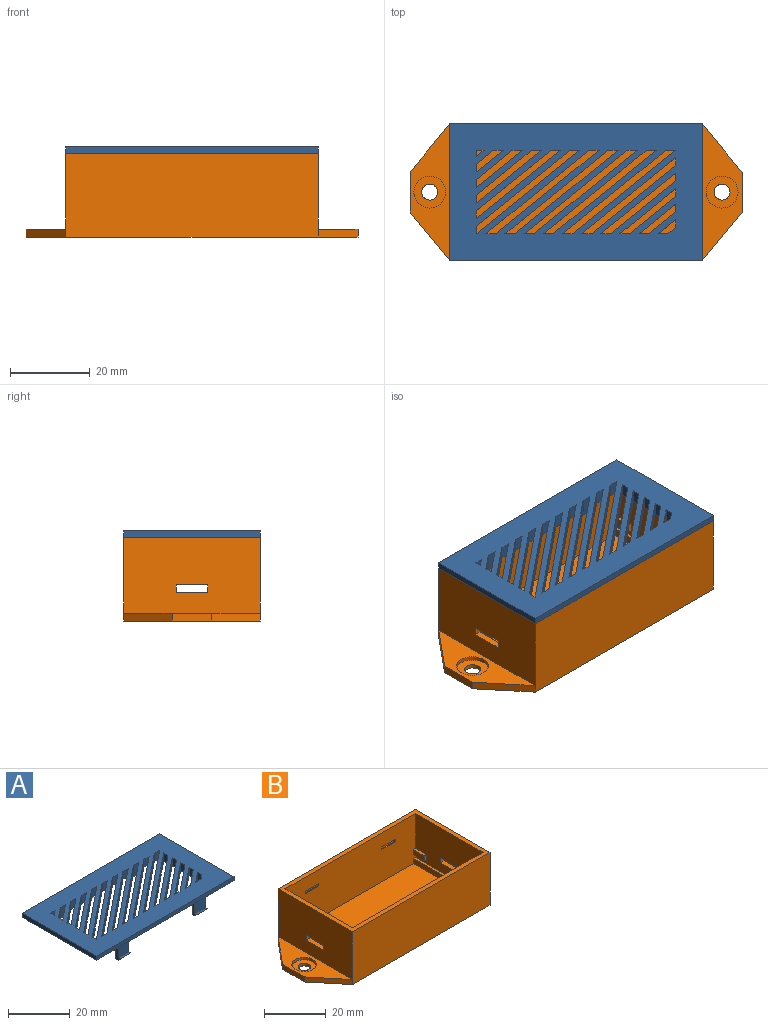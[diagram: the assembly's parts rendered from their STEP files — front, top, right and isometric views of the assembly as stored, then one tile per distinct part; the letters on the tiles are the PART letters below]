
ASSEMBLY  parts=2 mates=1
PART A: 98 faces, bbox 63.2x34.2x8.2 mm
  f0: plane 60x31mm, normal (0,0,-1), area 1312mm2, adj f2,f3,f9,f10,f11,f12,f13,f15
  f1: plane 63.2x34.2mm, normal (0,0,1), area 1636.4mm2, adj f5,f6,f7,f8,f35,f36,f37,f38
  f2: plane 60x5.6mm, normal (0,1,0), area 134.4mm2, adj f0,f4,f9,f10,f19,f21,f23,f24
  f3: plane 60x5.6mm, normal (0,-1,0), area 134.4mm2, adj f0,f4,f9,f10,f11,f13,f15,f16
  f4: plane 63.2x34.2mm, normal (0,0,-1), area 301.4mm2, adj f2,f3,f5,f6,f7,f8,f9,f10
  f5: plane 63.2x1.6mm, normal (0,-1,0), area 101.1mm2, adj f1,f4,f6,f8
  f6: plane 34.2x1.6mm, normal (1,0,0), area 54.7mm2, adj f1,f4,f5,f7
  f7: plane 63.2x1.6mm, normal (0,1,0), area 101.1mm2, adj f1,f4,f6,f8
  f8: plane 34.2x1.6mm, normal (-1,0,0), area 54.7mm2, adj f1,f4,f5,f7
  f9: plane 31x1.6mm, normal (1,0,0), area 49.6mm2, adj f0,f2,f3,f4
  f10: plane 31x1.6mm, normal (-1,0,0), area 49.6mm2, adj f0,f2,f3,f4
  f11: plane 5x2.2mm, normal (-1,0,0), area 6.5mm2, adj f0,f3,f12,f14,f33,f34
  f12: plane 5x4.8mm, normal (0,1,0), area 24mm2, adj f0,f11,f13,f14
  f13: plane 5x2.2mm, normal (1,0,0), area 6.5mm2, adj f0,f3,f12,f14,f33,f34
  f14: plane 4.8x1.2mm, normal (0,0,-1), area 5.8mm2, adj f11,f12,f13,f34
  f15: plane 5x2.2mm, normal (1,0,0), area 6.5mm2, adj f0,f3,f17,f18,f27,f28
  f16: plane 5x2.2mm, normal (-1,0,0), area 6.5mm2, adj f0,f3,f17,f18,f27,f28
  f17: plane 5x4.8mm, normal (0,1,0), area 24mm2, adj f0,f15,f16,f18
  f18: plane 4.8x1.2mm, normal (0,0,-1), area 5.8mm2, adj f15,f16,f17,f28
  f19: plane 5x2.2mm, normal (1,0,0), area 6.5mm2, adj f0,f2,f20,f22,f29,f30
  f20: plane 5x4.8mm, normal (0,-1,0), area 24mm2, adj f0,f19,f21,f22
  f21: plane 5x2.2mm, normal (-1,0,0), area 6.5mm2, adj f0,f2,f20,f22,f29,f30
  f22: plane 4.8x1.2mm, normal (0,0,-1), area 5.8mm2, adj f19,f20,f21,f30
  f23: plane 5x2.2mm, normal (-1,0,0), area 6.5mm2, adj f0,f2,f25,f26,f31,f32
  f24: plane 5x2.2mm, normal (1,0,0), area 6.5mm2, adj f0,f2,f25,f26,f31,f32
  f25: plane 5x4.8mm, normal (0,-1,0), area 24mm2, adj f0,f23,f24,f26
  f26: plane 4.8x1.2mm, normal (0,0,-1), area 5.8mm2, adj f23,f24,f25,f32
  f27: plane 4.8x1mm, normal (0,0,1), area 4.8mm2, adj f3,f15,f16,f28
  f28: plane 4.8x1mm, normal (0,-0.71,-0.71), area 6.8mm2, adj f15,f16,f18,f27
  f29: plane 4.8x1mm, normal (0,0,1), area 4.8mm2, adj f2,f19,f21,f30
  f30: plane 4.8x1mm, normal (0,0.71,-0.71), area 6.8mm2, adj f19,f21,f22,f29
  f31: plane 4.8x1mm, normal (0,0,1), area 4.8mm2, adj f2,f23,f24,f32
  f32: plane 4.8x1mm, normal (0,0.71,-0.71), area 6.8mm2, adj f23,f24,f26,f31
  f33: plane 4.8x1mm, normal (0,0,1), area 4.8mm2, adj f3,f11,f13,f34
  f34: plane 4.8x1mm, normal (0,-0.71,-0.71), area 6.8mm2, adj f11,f13,f14,f33
  f35: plane 3.2x2mm, normal (-0.63,0.78,0), area 8.2mm2, adj f0,f1,f36,f37
  f36: plane 3.2x1.62mm, normal (1,0,0), area 5.2mm2, adj f0,f1,f35,f37
  f37: plane 3.2x2mm, normal (0,-1,0), area 6.4mm2, adj f0,f1,f35,f36
  f38: plane 3.2x2.4mm, normal (0,1,0), area 7.7mm2, adj f0,f1,f39,f41
  f39: plane 23.6x19.06mm, normal (0.63,-0.78,0), area 97.1mm2, adj f0,f1,f38,f40
  f40: plane 3.2x1.94mm, normal (-1,0,0), area 6.2mm2, adj f0,f1,f39,f41
  f41: plane 21.2x17.12mm, normal (-0.63,0.78,0), area 87.2mm2, adj f0,f1,f38,f40
  f42: plane 3.2x2.4mm, normal (0,1,0), area 7.7mm2, adj f0,f1,f43,f45
  f43: plane 18.8x15.18mm, normal (0.63,-0.78,0), area 77.3mm2, adj f0,f1,f42,f44
  f44: plane 3.2x1.94mm, normal (-1,0,0), area 6.2mm2, adj f0,f1,f43,f45
  f45: plane 16.4x13.25mm, normal (-0.63,0.78,0), area 67.5mm2, adj f0,f1,f42,f44
  f46: plane 3.2x2.4mm, normal (0,1,0), area 7.7mm2, adj f0,f1,f47,f49
  f47: plane 26x21mm, normal (0.63,-0.78,0), area 106.9mm2, adj f0,f1,f46,f48
  f48: plane 3.2x2.4mm, normal (0,-1,0), area 7.7mm2, adj f0,f1,f47,f49
  f49: plane 26x21mm, normal (-0.63,0.78,0), area 106.9mm2, adj f0,f1,f46,f48
  f50: plane 26x21mm, normal (-0.63,0.78,0), area 106.9mm2, adj f0,f1,f51,f53
  f51: plane 3.2x2.4mm, normal (0,1,0), area 7.7mm2, adj f0,f1,f50,f52
  f52: plane 26x21mm, normal (0.63,-0.78,0), area 106.9mm2, adj f0,f1,f51,f53
  f53: plane 3.2x2.4mm, normal (0,-1,0), area 7.7mm2, adj f0,f1,f50,f52
  f54: plane 3.2x2.4mm, normal (0,1,0), area 7.7mm2, adj f0,f1,f55,f57
  f55: plane 4.4x3.55mm, normal (0.63,-0.78,0), area 18.1mm2, adj f0,f1,f54,f56
  f56: plane 3.2x1.94mm, normal (-1,0,0), area 6.2mm2, adj f0,f1,f55,f57
  f57: plane 3.2x2mm, normal (-0.63,0.78,0), area 8.2mm2, adj f0,f1,f54,f56
  f58: plane 3.2x2.4mm, normal (0,1,0), area 7.7mm2, adj f0,f1,f59,f61
  f59: plane 14x11.31mm, normal (0.63,-0.78,0), area 57.6mm2, adj f0,f1,f58,f60
  f60: plane 3.2x1.94mm, normal (-1,0,0), area 6.2mm2, adj f0,f1,f59,f61
  f61: plane 11.6x9.37mm, normal (-0.63,0.78,0), area 47.7mm2, adj f0,f1,f58,f60
  f62: plane 3.2x2.4mm, normal (0,1,0), area 7.7mm2, adj f0,f1,f63,f65
  f63: plane 9.2x7.43mm, normal (0.63,-0.78,0), area 37.8mm2, adj f0,f1,f62,f64
  f64: plane 3.2x1.94mm, normal (-1,0,0), area 6.2mm2, adj f0,f1,f63,f65
  f65: plane 6.8x5.49mm, normal (-0.63,0.78,0), area 28mm2, adj f0,f1,f62,f64
  f66: plane 14x11.31mm, normal (0.63,-0.78,0), area 57.6mm2, adj f0,f1,f67,f69
  f67: plane 3.2x2.4mm, normal (0,-1,0), area 7.7mm2, adj f0,f1,f66,f68
  f68: plane 16.4x13.25mm, normal (-0.63,0.78,0), area 67.5mm2, adj f0,f1,f67,f69
  f69: plane 3.2x1.94mm, normal (1,0,0), area 6.2mm2, adj f0,f1,f66,f68
  f70: plane 18.8x15.18mm, normal (0.63,-0.78,0), area 77.3mm2, adj f0,f1,f71,f73
  f71: plane 3.2x2.4mm, normal (0,-1,0), area 7.7mm2, adj f0,f1,f70,f72
  f72: plane 21.2x17.12mm, normal (-0.63,0.78,0), area 87.2mm2, adj f0,f1,f71,f73
  f73: plane 3.2x1.94mm, normal (1,0,0), area 6.2mm2, adj f0,f1,f70,f72
  f74: plane 4.4x3.55mm, normal (0.63,-0.78,0), area 18.1mm2, adj f0,f1,f75,f77
  f75: plane 3.2x2.4mm, normal (0,-1,0), area 7.7mm2, adj f0,f1,f74,f76
  f76: plane 6.8x5.49mm, normal (-0.63,0.78,0), area 28mm2, adj f0,f1,f75,f77
  f77: plane 3.2x1.94mm, normal (1,0,0), area 6.2mm2, adj f0,f1,f74,f76
  f78: plane 9.2x7.43mm, normal (0.63,-0.78,0), area 37.8mm2, adj f0,f1,f79,f81
  f79: plane 3.2x2.4mm, normal (0,-1,0), area 7.7mm2, adj f0,f1,f78,f80
  f80: plane 11.6x9.37mm, normal (-0.63,0.78,0), area 47.7mm2, adj f0,f1,f79,f81
  f81: plane 3.2x1.94mm, normal (1,0,0), area 6.2mm2, adj f0,f1,f78,f80
  f82: plane 3.2x2.4mm, normal (0,1,0), area 7.7mm2, adj f0,f1,f83,f85
  f83: plane 26x21mm, normal (0.63,-0.78,0), area 106.9mm2, adj f0,f1,f82,f84
  f84: plane 3.2x2.4mm, normal (0,-1,0), area 7.7mm2, adj f0,f1,f83,f85
  f85: plane 26x21mm, normal (-0.63,0.78,0), area 106.9mm2, adj f0,f1,f82,f84
  f86: plane 3.2x2.4mm, normal (0,1,0), area 7.7mm2, adj f0,f1,f87,f89
  f87: plane 26x21mm, normal (0.63,-0.78,0), area 106.9mm2, adj f0,f1,f86,f88
  f88: plane 3.2x2.4mm, normal (0,-1,0), area 7.7mm2, adj f0,f1,f87,f89
  f89: plane 26x21mm, normal (-0.63,0.78,0), area 106.9mm2, adj f0,f1,f86,f88
  f90: plane 26x21mm, normal (-0.63,0.78,0), area 106.9mm2, adj f0,f1,f91,f93
  f91: plane 3.2x1.94mm, normal (1,0,0), area 6.2mm2, adj f0,f1,f90,f92
  f92: plane 23.6x19.06mm, normal (0.63,-0.78,0), area 97.1mm2, adj f0,f1,f91,f93
  f93: plane 3.2x2.4mm, normal (0,-1,0), area 7.7mm2, adj f0,f1,f90,f92
  f94: plane 3.2x2.4mm, normal (0,1,0), area 7.7mm2, adj f0,f1,f95,f97
  f95: plane 26x21mm, normal (0.63,-0.78,0), area 106.9mm2, adj f0,f1,f94,f96
  f96: plane 3.2x2.4mm, normal (0,-1,0), area 7.7mm2, adj f0,f1,f95,f97
  f97: plane 26x21mm, normal (-0.63,0.78,0), area 106.9mm2, adj f0,f1,f94,f96
PART B: 71 faces, bbox 83.2x34.2x21 mm
  f0: plane 5x2mm, normal (-1,0,0), area 10mm2, adj f1,f2,f4,f70
  f1: plane 5x1mm, normal (0,0,-1), area 5mm2, adj f0,f4,f7,f70
  f2: plane 5x1mm, normal (0,0,1), area 5mm2, adj f0,f4,f7,f70
  f3: plane 5x1mm, normal (0,0,1), area 5mm2, adj f7,f12,f61,f69
  f4: plane 60x19.4mm, normal (0,1,0), area 1144.8mm2, adj f0,f1,f2,f7,f8,f9,f14,f27
  f5: plane 5x1mm, normal (0,0,-1), area 5mm2, adj f6,f9,f12,f58
  f6: plane 5x1.5mm, normal (0.83,0,0.55), area 9mm2, adj f5,f9,f12,f58
  f7: plane 31x17.4mm, normal (-1,0,0), area 503.4mm2, adj f1,f2,f3,f4,f12,f14,f53,f59
  f8: plane 58x31mm, normal (0,0,1), area 1798mm2, adj f4,f12,f52,f54
  f9: plane 31x17.4mm, normal (1,0,0), area 508.4mm2, adj f4,f5,f6,f12,f14,f51,f55,f56
  f10: plane 34.2x19mm, normal (1,0,0), area 633.8mm2, adj f14,f15,f16,f44,f60,f66,f67,f68
  f11: plane 34.2x19mm, normal (-1,0,0), area 633.8mm2, adj f14,f15,f16,f40,f62,f63,f64,f65
  f12: plane 60x19.4mm, normal (0,-1,0), area 1144.8mm2, adj f3,f5,f6,f7,f8,f9,f14,f17
  f13: plane 83.2x34.2mm, normal (0,0,-1), area 2578.3mm2, adj f15,f16,f37,f38,f39,f41,f42,f43
  f14: plane 63.2x34.2mm, normal (0,0,1), area 301.4mm2, adj f4,f7,f9,f10,f11,f12,f15,f16
  f15: plane 63.2x21mm, normal (0,-1,0), area 1327.2mm2, adj f10,f11,f13,f14,f37,f41
  f16: plane 63.2x21mm, normal (0,1,0), area 1327.2mm2, adj f10,f11,f13,f14,f39,f42
  f17: plane 1x0.4mm, normal (-1,0,0), area 0.4mm2, adj f12,f18,f20,f21
  f18: plane 6.2x0.4mm, normal (0,0,-1), area 2.5mm2, adj f12,f17,f19,f21
  f19: plane 1x0.4mm, normal (1,0,0), area 0.4mm2, adj f12,f18,f20,f21
  f20: plane 6.2x0.4mm, normal (0,0,1), area 2.5mm2, adj f12,f17,f19,f21
  f21: plane 6.2x1mm, normal (0,-1,0), area 6.2mm2, adj f17,f18,f19,f20
  f22: plane 6.2x0.4mm, normal (0,0,-1), area 2.5mm2, adj f12,f23,f25,f26
  f23: plane 1x0.4mm, normal (1,0,0), area 0.4mm2, adj f12,f22,f24,f26
  f24: plane 6.2x0.4mm, normal (0,0,1), area 2.5mm2, adj f12,f23,f25,f26
  f25: plane 1x0.4mm, normal (-1,0,0), area 0.4mm2, adj f12,f22,f24,f26
  f26: plane 6.2x1mm, normal (0,-1,0), area 6.2mm2, adj f22,f23,f24,f25
  f27: plane 6.2x0.4mm, normal (0,0,-1), area 2.5mm2, adj f4,f28,f30,f31
  f28: plane 1x0.4mm, normal (-1,0,0), area 0.4mm2, adj f4,f27,f29,f31
  f29: plane 6.2x0.4mm, normal (0,0,1), area 2.5mm2, adj f4,f28,f30,f31
  f30: plane 1x0.4mm, normal (1,0,0), area 0.4mm2, adj f4,f27,f29,f31
  f31: plane 6.2x1mm, normal (0,1,0), area 6.2mm2, adj f27,f28,f29,f30
  f32: plane 1x0.4mm, normal (1,0,0), area 0.4mm2, adj f4,f33,f35,f36
  f33: plane 6.2x0.4mm, normal (0,0,-1), area 2.5mm2, adj f4,f32,f34,f36
  f34: plane 1x0.4mm, normal (-1,0,0), area 0.4mm2, adj f4,f33,f35,f36
  f35: plane 6.2x0.4mm, normal (0,0,1), area 2.5mm2, adj f4,f32,f34,f36
  f36: plane 6.2x1mm, normal (0,1,0), area 6.2mm2, adj f32,f33,f34,f35
  f37: plane 12.1x10mm, normal (-0.77,-0.64,0), area 31.4mm2, adj f13,f15,f38,f40
  f38: plane 10x2mm, normal (-1,0,0), area 20mm2, adj f13,f37,f39,f40
  f39: plane 12.1x10mm, normal (-0.77,0.64,0), area 31.4mm2, adj f13,f16,f38,f40
  f40: plane 34.2x10mm, normal (0,0,1), area 170.7mm2, adj f11,f37,f38,f39,f47
  f41: plane 12.1x10mm, normal (0.77,-0.64,0), area 31.4mm2, adj f13,f15,f43,f44
  f42: plane 12.1x10mm, normal (0.77,0.64,0), area 31.4mm2, adj f13,f16,f43,f44
  f43: plane 10x2mm, normal (1,0,0), area 20mm2, adj f13,f41,f42,f44
  f44: plane 34.2x10mm, normal (0,0,1), area 170.7mm2, adj f10,f41,f42,f43,f50
  f45: cylinder r=2mm len=4mm, axis (0,0,1), area 12.6mm2, adj f13,f46
  f46: plane 8x8mm, normal (0,0,1), area 37.7mm2, adj f45,f47
  f47: cylinder r=4mm len=8mm, axis (0,0,1), area 25.1mm2, adj f40,f46
  f48: cylinder r=2mm len=4mm, axis (0,0,1), area 12.6mm2, adj f13,f49
  f49: plane 8x8mm, normal (0,0,1), area 37.7mm2, adj f48,f50
  f50: cylinder r=4mm len=8mm, axis (0,0,1), area 25.1mm2, adj f44,f49
  f51: plane 31x1mm, normal (0,0,1), area 31mm2, adj f4,f9,f12,f52
  f52: plane 31x2mm, normal (1,0,0), area 62mm2, adj f4,f8,f12,f51
  f53: plane 31x1mm, normal (0,0,1), area 31mm2, adj f4,f7,f12,f54
  f54: plane 31x2mm, normal (-1,0,0), area 62mm2, adj f4,f8,f12,f53
  f55: plane 5x1mm, normal (0,0,-1), area 5mm2, adj f4,f9,f56,f57
  f56: plane 5x1.5mm, normal (0.83,0,0.55), area 9mm2, adj f4,f9,f55,f57
  f57: plane 1.5x1mm, normal (0,1,0), area 0.7mm2, adj f9,f55,f56
  f58: plane 1.5x1mm, normal (0,-1,0), area 0.7mm2, adj f5,f6,f9
  f59: plane 5x1mm, normal (0,0,-1), area 5mm2, adj f7,f12,f61,f69
  f60: plane 8x1.6mm, normal (0,0,1), area 12.8mm2, adj f7,f10,f66,f67
  f61: plane 5x2mm, normal (-1,0,0), area 10mm2, adj f3,f12,f59,f69
  f62: plane 8x1.6mm, normal (0,0,-1), area 12.8mm2, adj f9,f11,f63,f65
  f63: plane 2x1.6mm, normal (0,1,0), area 3.2mm2, adj f9,f11,f62,f64
  f64: plane 8x1.6mm, normal (0,0,1), area 12.8mm2, adj f9,f11,f63,f65
  f65: plane 2x1.6mm, normal (0,-1,0), area 3.2mm2, adj f9,f11,f62,f64
  f66: plane 2x1.6mm, normal (0,-1,0), area 3.2mm2, adj f7,f10,f60,f68
  f67: plane 2x1.6mm, normal (0,1,0), area 3.2mm2, adj f7,f10,f60,f68
  f68: plane 8x1.6mm, normal (0,0,-1), area 12.8mm2, adj f7,f10,f66,f67
  f69: plane 2x1mm, normal (0,-1,0), area 2mm2, adj f3,f7,f59,f61
  f70: plane 2x1mm, normal (0,1,0), area 2mm2, adj f0,f1,f2,f7
PLACE A t=(-0.12,-2.65,20.23)mm
PLACE B t=(-0.12,-2.65,-0.77)mm
MATE fastened A.f4 <-> B.f14  axis (0,0,-1) through (31.48,14.45,20.23)mm
